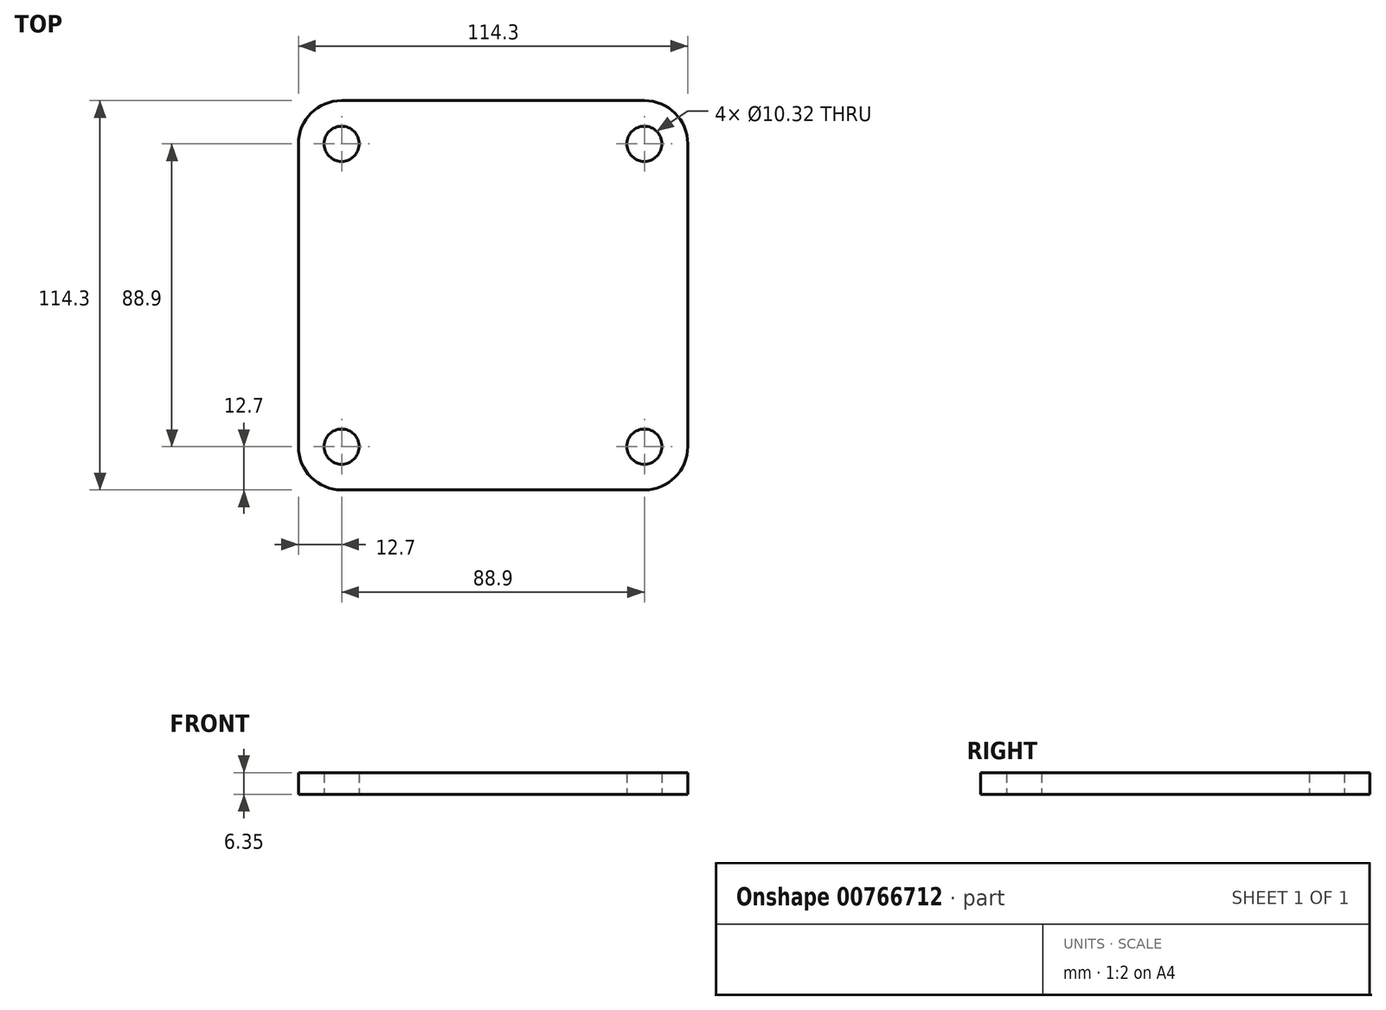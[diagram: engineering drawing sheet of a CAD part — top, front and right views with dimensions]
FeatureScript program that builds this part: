
annotation { "Feature Type Name" : "Feature", "Feature Type Description" : "" }
export const myFeature = defineFeature(function(context is Context, id is Id, definition is map)
    precondition{}
    {
        {
            var Q0;
            Q0=qCreatedBy(makeId("Top.planeOp"),FACE);
            var sketch = newSketch(context, id + "F0", { "sketchPlane" : qUnion([Q0])});
            skLineSegment(sketch, "E0.bottom", {"start": v(12.7, 0) * mm, "end": v(101.6, 0) * mm});
            skLineSegment(sketch, "E0.top", {"start": v(12.7, -114.3) * mm, "end": v(101.6, -114.3) * mm});
            skLineSegment(sketch, "E0.left", {"start": v(0, -12.7) * mm, "end": v(0, -101.6) * mm});
            skLineSegment(sketch, "E0.right", {"start": v(114.3, -12.7) * mm, "end": v(114.3, -101.6) * mm});
            skPoint(sketch, "E1.visualSharp", {"position": v(0, 0) * mm});
            skArc(sketch, "E1.filletArc", {"start": v(12.7, 0) * mm, "mid": v(3.72, -3.72) * mm, "end": v(0, -12.7) * mm});
            skPoint(sketch, "E2.visualSharp", {"position": v(114.3, 0) * mm});
            skArc(sketch, "E2.filletArc", {"start": v(114.3, -12.7) * mm, "mid": v(110.58, -3.72) * mm, "end": v(101.6, 0) * mm});
            skPoint(sketch, "E3.visualSharp", {"position": v(0, -114.3) * mm});
            skArc(sketch, "E3.filletArc", {"start": v(0, -101.6) * mm, "mid": v(3.72, -110.58) * mm, "end": v(12.7, -114.3) * mm});
            skPoint(sketch, "E4.visualSharp", {"position": v(114.3, -114.3) * mm});
            skArc(sketch, "E4.filletArc", {"start": v(101.6, -114.3) * mm, "mid": v(110.58, -110.58) * mm, "end": v(114.3, -101.6) * mm});
            skCircle(sketch, "E5", {"center": v(101.6, -12.7) * mm, "radius": 5.16 * mm});
            skCircle(sketch, "E6", {"center": v(101.6, -101.6) * mm, "radius": 5.16 * mm});
            skCircle(sketch, "E7", {"center": v(12.7, -101.6) * mm, "radius": 5.16 * mm});
            skCircle(sketch, "E8", {"center": v(12.7, -12.7) * mm, "radius": 5.16 * mm});
            skSolve(sketch);
        }
        {
            var Q0;
            Q0=makeQuery(id+"F0.imprint","IMPRINT",FACE,{"disambiguationData":[TD([[makeQuery(id+"F0.imprint","IMPRINT",EDGE,{"derivedFrom":sQuery(id+"F0.wireOp",EDGE,"E0.bottom")}),-1.0]])]});
            extrude(context, id + "F1", {"entities" : qUnion([Q0]), "depth" : 6.35 * mm, "offsetDistance" : 25.4 * mm});
        }
    });
